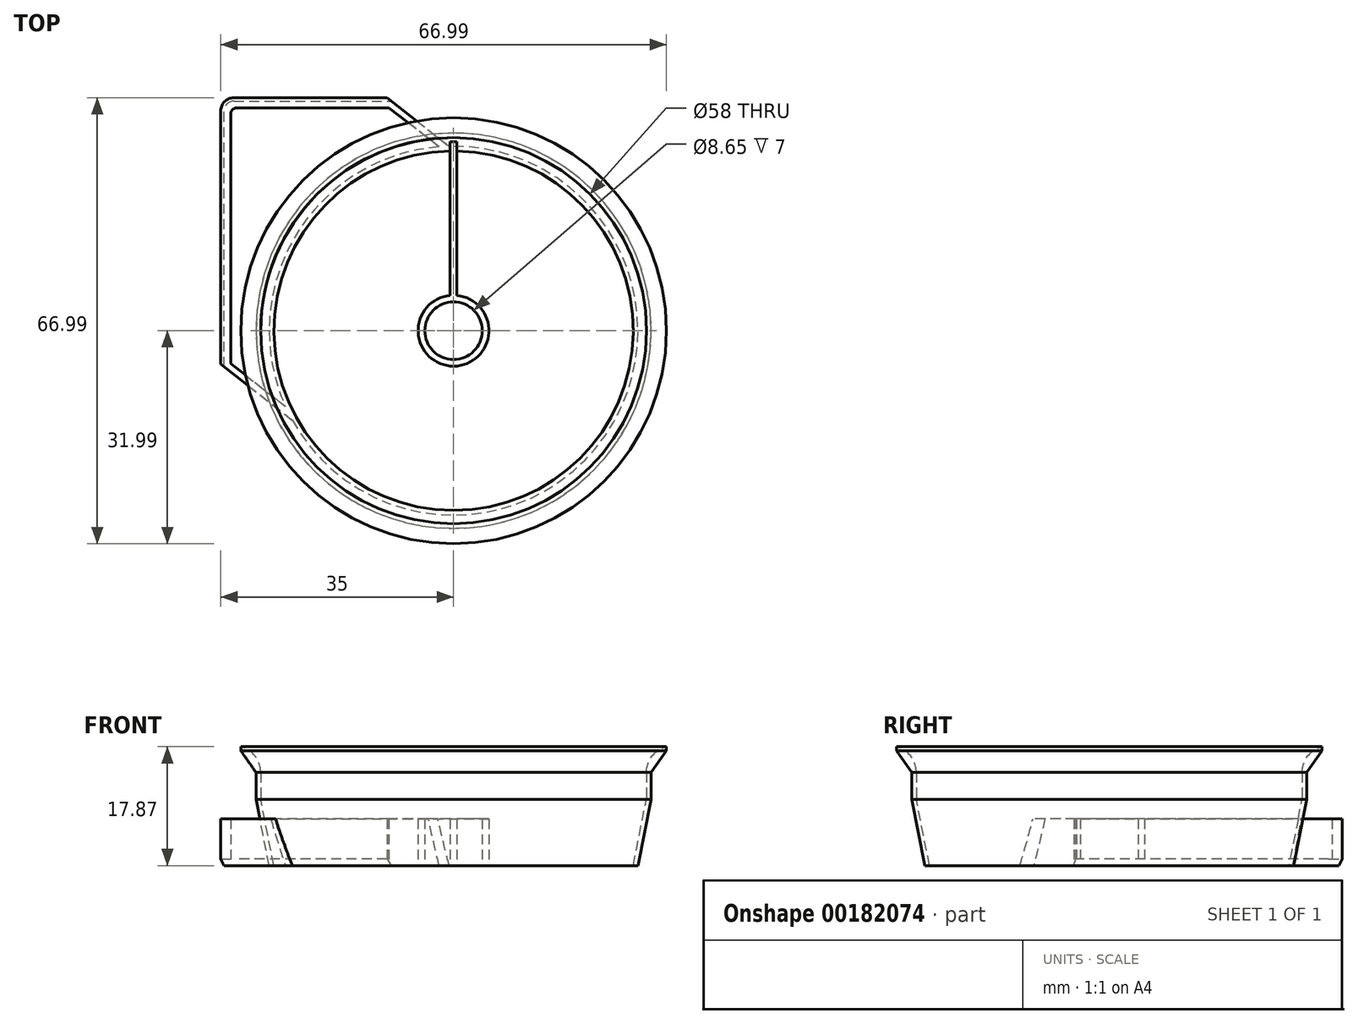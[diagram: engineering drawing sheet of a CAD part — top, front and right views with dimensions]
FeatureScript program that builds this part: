
annotation { "Feature Type Name" : "Feature", "Feature Type Description" : "" }
export const myFeature = defineFeature(function(context is Context, id is Id, definition is map)
    precondition{}
    {
        {
            var Q0;
            Q0=qCreatedBy(makeId("Front.planeOp"),FACE);
            cPlane(context, id + "F0", {"entities" : qUnion([Q0]), "cplaneType" : CPlaneType.OFFSET, "offset" : 35 * mm, "width" : 150 * mm, "height" : 150 * mm});
        }
        {
            var Q0;
            Q0=qCreatedBy(id+"F0.planeOp",FACE);
            var sketch = newSketch(context, id + "F1", { "sketchPlane" : qUnion([Q0])});
            skLineSegment(sketch, "E0", {"start": v(35, 0) * mm, "end": v(35, 30.59) * mm, "construction": true});
            skPoint(sketch, "E1.visualSharp", {"position": v(60.13, 14.33) * mm});
            skArc(sketch, "E1.filletArc", {"start": v(66.99, 17.87) * mm, "mid": v(64.83, 16.45) * mm, "end": v(64, 14) * mm});
            skLineSegment(sketch, "E2.trimOffspring", {"start": v(64.7, 9.93) * mm, "end": v(64.7, 14) * mm});
            skLineSegment(sketch, "E3", {"start": v(64.7, 14) * mm, "end": v(66.99, 17.27) * mm});
            skLineSegment(sketch, "E4", {"start": v(66.99, 17.27) * mm, "end": v(66.99, 17.87) * mm});
            skLineSegment(sketch, "E5", {"start": v(64, 14) * mm, "end": v(64, 10) * mm});
            skLineSegment(sketch, "E6", {"start": v(64, 10) * mm, "end": v(62, 0) * mm});
            skLineSegment(sketch, "E7", {"start": v(62, 0) * mm, "end": v(62.71, 0) * mm});
            skLineSegment(sketch, "E8", {"start": v(62.71, 0) * mm, "end": v(64.7, 9.93) * mm});
            skSolve(sketch);
        }
        {
            var Q0;
            Q0=makeQuery(id+"F1.imprint","IMPRINT",FACE,{"disambiguationData":[TD([[makeQuery(id+"F1.imprint","IMPRINT",EDGE,{"derivedFrom":sQuery(id+"F1.wireOp",EDGE,"E1.filletArc")}),1.0]])]});
            var Q1;
            Q1=sQuery(id+"F1.wireOp",EDGE,"vP0waRYa-sEjs-OOEK-19TI-QNroBSpxUcqd");
            var Q2;
            Q2=sQuery(id+"F1.wireOp",EDGE,"E1.filletArc");
            var Q3;
            Q3=sQuery(id+"F1.wireOp",EDGE,"MQNye80a-Q02t-6oJt-o7DE-eQ2WEElS9EKd");
            var Q4;
            Q4=sQuery(id+"F1.wireOp",EDGE,"E0");
            revolve(context, id + "F2", {"entities" : qUnion([Q0]), "surfaceEntities" : qUnion([Q1, Q2, Q3]), "axis" : qUnion([Q4]), "revolveType" : RevolveType.FULL});
        }
        {
            var Q0;
            Q0=qCreatedBy(makeId("Top.planeOp"),FACE);
            var sketch = newSketch(context, id + "F3", { "sketchPlane" : qUnion([Q0])});
            skLineSegment(sketch, "E9.bottom", {"start": v(34.5, -30.53) * mm, "end": v(35.5, -30.53) * mm});
            skLineSegment(sketch, "E9.top", {"start": v(34.5, -7.5) * mm, "end": v(35.5, -7.5) * mm});
            skLineSegment(sketch, "E9.left", {"start": v(34.5, -30.53) * mm, "end": v(34.5, -7.5) * mm});
            skLineSegment(sketch, "E9.right", {"start": v(35.5, -30.53) * mm, "end": v(35.5, -7.5) * mm});
            skCircle(sketch, "E10", {"center": v(35, -35) * mm, "radius": 4.5 * mm, "construction": true});
            skLineSegment(sketch, "E11", {"start": v(35, -35) * mm, "end": v(35, -12.05) * mm, "construction": true});
            skSolve(sketch);
        }
        {
            var Q0;
            Q0=makeQuery(id+"F3.imprint","IMPRINT",FACE,{"disambiguationData":[TD([[makeQuery(id+"F3.imprint","IMPRINT",EDGE,{"derivedFrom":sQuery(id+"F3.wireOp",EDGE,"E9.bottom")}),1.0]])]});
            extrude(context, id + "F4", {"entities" : qUnion([Q0]), "operationType" : NewBodyOperationType.ADD, "depth" : 7 * mm});
        }
        {
            var Q0;
            Q0=qCreatedBy(makeId("Top.planeOp"),FACE);
            var sketch = newSketch(context, id + "F5", { "sketchPlane" : qUnion([Q0])});
            skCircle(sketch, "E12", {"center": v(35, -35) * mm, "radius": 4.33 * mm});
            skCircle(sketch, "E13", {"center": v(35, -35) * mm, "radius": 5.33 * mm});
            skSolve(sketch);
        }
        {
            var Q0;
            Q0=makeQuery(id+"F5.imprint","IMPRINT",FACE,{"disambiguationData":[TD([[makeQuery(id+"F5.imprint","IMPRINT",EDGE,{"derivedFrom":sQuery(id+"F5.wireOp",EDGE,"E12")}),-1.0]])]});
            extrude(context, id + "F6", {"entities" : qUnion([Q0]), "operationType" : NewBodyOperationType.ADD, "depth" : 7 * mm});
        }
        {
            var Q0;
            Q0=makeQuery(id+"F4.opExtrude","SWEPT_FACE",FACE,{"disambiguationData":[OSD([sQuery(id+"F3.wireOp",EDGE,"E9.top")])]});
            extrude(context, id + "F7", {"entities" : qUnion([Q0]), "operationType" : NewBodyOperationType.ADD, "endBound" : BoundingType.UP_TO_NEXT, "depth" : 25 * mm});
        }
        {
            var Q0;
            Q0=qCreatedBy(makeId("Top.planeOp"),FACE);
            var sketch = newSketch(context, id + "F8", { "sketchPlane" : qUnion([Q0])});
            skLineSegment(sketch, "E14", {"start": v(0, 0) * mm, "end": v(0, 0) * mm});
            skLineSegment(sketch, "E15", {"start": v(25, 0) * mm, "end": v(31.98, -5.45) * mm});
            skLineSegment(sketch, "E16", {"start": v(0, 0) * mm, "end": v(0, -40.04) * mm});
            skLineSegment(sketch, "E17", {"start": v(0, -40.04) * mm, "end": v(7.31, -45.75) * mm});
            skLineSegment(sketch, "E18", {"start": v(0, 0) * mm, "end": v(25, 0) * mm});
            skLineSegment(sketch, "E19", {"start": v(31.36, -6.24) * mm, "end": v(25.3, -1.5) * mm});
            skLineSegment(sketch, "E20", {"start": v(25.3, -1.5) * mm, "end": v(1.5, -1.5) * mm});
            skLineSegment(sketch, "E21", {"start": v(1.5, -1.5) * mm, "end": v(1.5, -39.94) * mm});
            skLineSegment(sketch, "E22", {"start": v(1.5, -39.94) * mm, "end": v(7.93, -44.96) * mm});
            skLineSegment(sketch, "E23", {"start": v(31.36, -6.24) * mm, "end": v(31.98, -5.45) * mm});
            skLineSegment(sketch, "E24", {"start": v(7.31, -45.75) * mm, "end": v(7.93, -44.96) * mm});
            skSolve(sketch);
        }
        {
            var Q0;
            Q0=makeQuery(id+"F8.imprint","IMPRINT",FACE,{"disambiguationData":[TD([[makeQuery(id+"F8.imprint","IMPRINT",EDGE,{"derivedFrom":sQuery(id+"F8.wireOp",EDGE,"E15")}),-1.0]])]});
            extrude(context, id + "F9", {"entities" : qUnion([Q0]), "operationType" : NewBodyOperationType.ADD, "depth" : 7 * mm});
        }
        {
            var Q0;
            Q0=makeQuery(id+"F9.opExtrude","SWEPT_FACE",FACE,{"disambiguationData":[OSD([sQuery(id+"F8.wireOp",EDGE,"E23")])]});
            extrude(context, id + "F10", {"entities" : qUnion([Q0]), "operationType" : NewBodyOperationType.ADD, "endBound" : BoundingType.UP_TO_NEXT, "depth" : 25 * mm});
        }
        {
            var Q0;
            Q0=makeQuery(id+"F9.opExtrude","SWEPT_FACE",FACE,{"disambiguationData":[OSD([sQuery(id+"F8.wireOp",EDGE,"E24")])]});
            extrude(context, id + "F11", {"entities" : qUnion([Q0]), "operationType" : NewBodyOperationType.ADD, "endBound" : BoundingType.UP_TO_NEXT, "depth" : 25 * mm});
        }
        {
            var Q0;
            Q0=makeQuery(id+"F9.opExtrude","SWEPT_EDGE",EDGE,{"disambiguationData":[OSD([sQuery(id+"F8.wireOp",EDGE,"E16"),sQuery(id+"F8.wireOp",EDGE,"E18")])]});
            fillet(context, id + "F12", {"entities" : qUnion([Q0]), "radius" : 2 * mm, "tangentPropagation" : true, "allowEdgeOverflow" : false});
        }
        {
            var Q0;
            Q0=makeQuery(id+"F9.opExtrude","SWEPT_EDGE",EDGE,{"disambiguationData":[OSD([sQuery(id+"F8.wireOp",EDGE,"E20"),sQuery(id+"F8.wireOp",EDGE,"E21")])]});
            fillet(context, id + "F13", {"entities" : qUnion([Q0]), "radius" : 1 * mm, "tangentPropagation" : true, "allowEdgeOverflow" : false});
        }
        {
            var Q0;
            Q0=makeQuery(id+"F9.opExtrude","CAP_EDGE",EDGE,{"disambiguationData":[OSD([sQuery(id+"F8.wireOp",EDGE,"E18")])],"isStart":true});
            chamfer(context, id + "F14", {"entities" : qUnion([Q0]), "chamferType" : ChamferType.TWO_OFFSETS, "width1" : .5 * mm, "oppositeDirection" : false, "width2" : 1 * mm, "tangentPropagation" : true});
        }
    });
